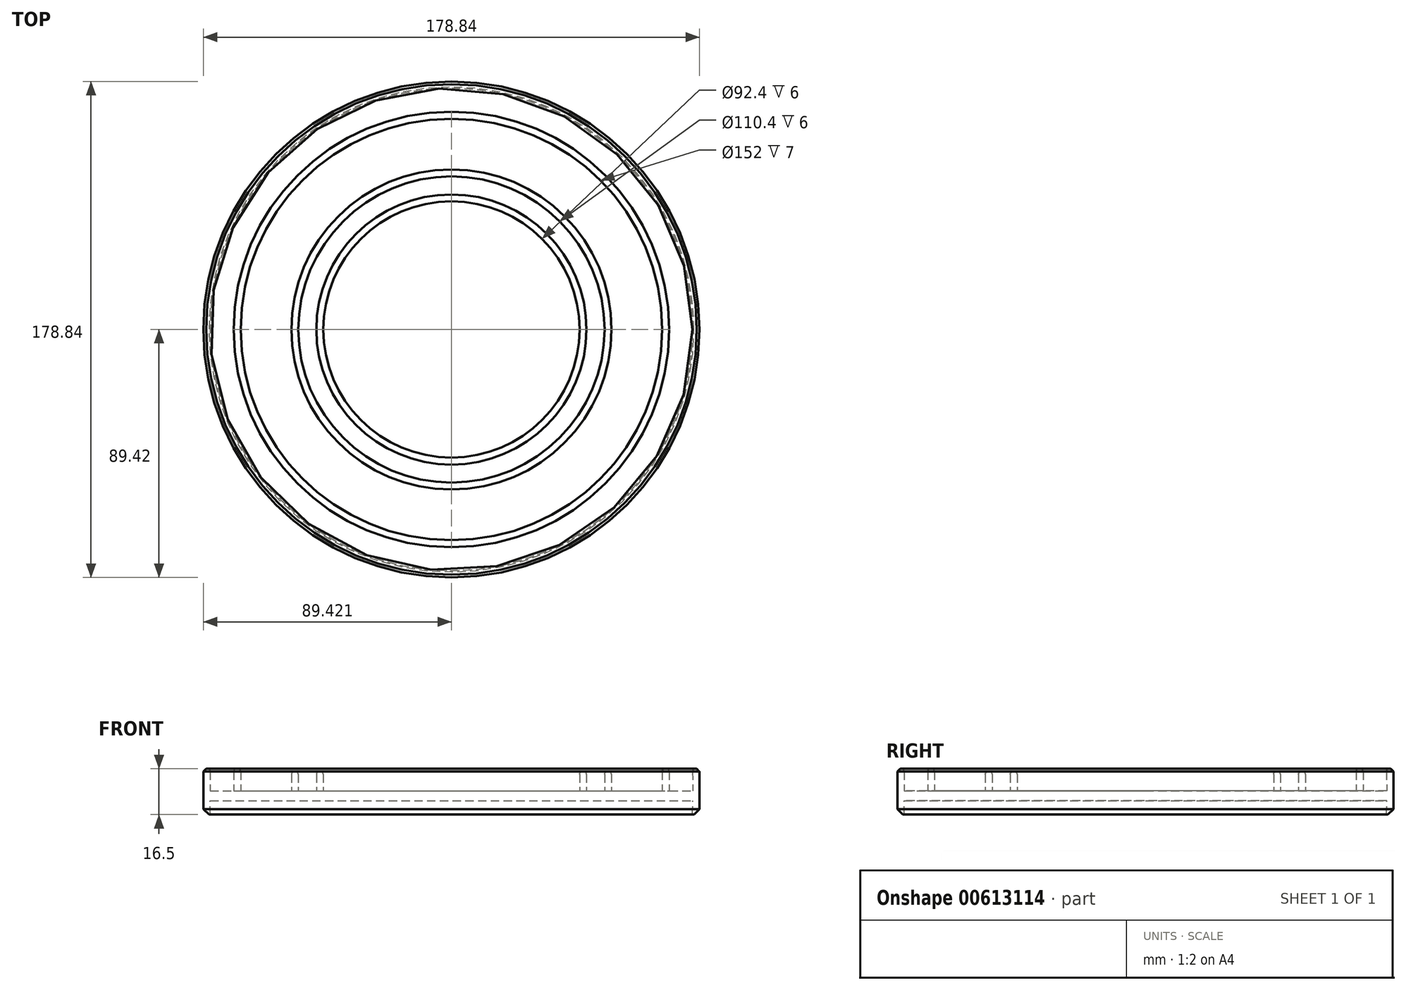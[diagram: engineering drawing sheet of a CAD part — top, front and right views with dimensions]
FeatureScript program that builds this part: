
annotation { "Feature Type Name" : "Feature", "Feature Type Description" : "" }
export const myFeature = defineFeature(function(context is Context, id is Id, definition is map)
    precondition{}
    {
        {
            var Q0;
            Q0=qCreatedBy(makeId("Front.planeOp"),FACE);
            var sketch = newSketch(context, id + "F0", { "sketchPlane" : qUnion([Q0])});
            skLineSegment(sketch, "E0", {"start": v(-51.63, -13.29) * mm, "end": v(-51.63, -9.79) * mm});
            skLineSegment(sketch, "E1", {"start": v(-51.63, -9.79) * mm, "end": v(-51.63, -1.79) * mm});
            skLineSegment(sketch, "E2", {"start": v(-51.63, -1.79) * mm, "end": v(-49.13, -1.79) * mm});
            skLineSegment(sketch, "E3", {"start": v(-49.2, -13.29) * mm, "end": v(37.8, -13.29) * mm});
            skLineSegment(sketch, "E4", {"start": v(37.8, -13.29) * mm, "end": v(37.8, -9.79) * mm});
            skLineSegment(sketch, "E5", {"start": v(37.8, -9.79) * mm, "end": v(-8.4, -9.79) * mm});
            skLineSegment(sketch, "E6", {"start": v(-8.4, -9.79) * mm, "end": v(-8.4, -2.79) * mm});
            skLineSegment(sketch, "E7", {"start": v(-8.4, -2.79) * mm, "end": v(-10.9, -2.79) * mm});
            skLineSegment(sketch, "E8", {"start": v(-10.9, -2.79) * mm, "end": v(-10.9, -9.79) * mm});
            skLineSegment(sketch, "E9", {"start": v(-10.9, -9.79) * mm, "end": v(-17.4, -9.79) * mm});
            skLineSegment(sketch, "E10", {"start": v(-17.4, -9.79) * mm, "end": v(-17.4, -2.79) * mm});
            skLineSegment(sketch, "E11", {"start": v(-17.4, -2.79) * mm, "end": v(-19.9, -2.79) * mm});
            skLineSegment(sketch, "E12", {"start": v(-19.9, -2.79) * mm, "end": v(-19.9, -9.79) * mm});
            skLineSegment(sketch, "E13", {"start": v(-19.9, -9.79) * mm, "end": v(-38.2, -9.79) * mm});
            skLineSegment(sketch, "E14", {"start": v(-38.2, -9.79) * mm, "end": v(-38.2, -1.79) * mm});
            skLineSegment(sketch, "E15", {"start": v(-38.2, -1.79) * mm, "end": v(-40.7, -1.79) * mm});
            skLineSegment(sketch, "E16", {"start": v(-40.7, -1.79) * mm, "end": v(-40.7, -9.79) * mm});
            skLineSegment(sketch, "E17", {"start": v(-40.7, -9.79) * mm, "end": v(-49.2, -9.79) * mm});
            skLineSegment(sketch, "E18", {"start": v(-49.13, -1.79) * mm, "end": v(-49.2, -9.79) * mm});
            skLineSegment(sketch, "E19", {"start": v(-51.63, -13.29) * mm, "end": v(-51.63, -18.29) * mm});
            skLineSegment(sketch, "E20", {"start": v(-51.63, -18.29) * mm, "end": v(-49.13, -18.29) * mm});
            skLineSegment(sketch, "E21", {"start": v(-49.13, -18.29) * mm, "end": v(-49.2, -13.29) * mm});
            skSolve(sketch);
        }
        {
            var Q0;
            Q0=makeQuery(id+"F0.imprint","IMPRINT",FACE,{"disambiguationData":[TD([[makeQuery(id+"F0.imprint","IMPRINT",EDGE,{"derivedFrom":sQuery(id+"F0.wireOp",EDGE,"E0")}),-1.0]])]});
            var Q1;
            Q1=sQuery(id+"F0.wireOp",EDGE,"E4");
            revolve(context, id + "F1", {"entities" : qUnion([Q0]), "axis" : qUnion([Q1]), "revolveType" : RevolveType.FULL});
        }
        {
            var Q0;
            Q0=makeQuery(id+"F1.opRevolve","SWEPT_EDGE",EDGE,{"disambiguationData":[OSD([sQuery(id+"F0.wireOp",EDGE,"E1"),sQuery(id+"F0.wireOp",EDGE,"E2")])]});
            chamfer(context, id + "F2", {"entities" : qUnion([Q0]), "width" : 1 * mm, "tangentPropagation" : true});
        }
        {
            var Q0;
            Q0=makeQuery(id+"F1.opRevolve","SWEPT_EDGE",EDGE,{"disambiguationData":[OSD([sQuery(id+"F0.wireOp",EDGE,"E2"),sQuery(id+"F0.wireOp",EDGE,"E18")])]});
            var Q1;
            Q1=makeQuery(id+"F1.opRevolve","SWEPT_FACE",FACE,{"disambiguationData":[OSD([sQuery(id+"F0.wireOp",EDGE,"E15")])]});
            var Q2;
            Q2=makeQuery(id+"F1.opRevolve","SWEPT_EDGE",EDGE,{"disambiguationData":[OSD([sQuery(id+"F0.wireOp",EDGE,"E11"),sQuery(id+"F0.wireOp",EDGE,"E12")])]});
            var Q3;
            Q3=makeQuery(id+"F1.opRevolve","SWEPT_EDGE",EDGE,{"disambiguationData":[OSD([sQuery(id+"F0.wireOp",EDGE,"E7"),sQuery(id+"F0.wireOp",EDGE,"E8")])]});
            var Q4;
            Q4=makeQuery(id+"F1.opRevolve","SWEPT_EDGE",EDGE,{"disambiguationData":[OSD([sQuery(id+"F0.wireOp",EDGE,"E6"),sQuery(id+"F0.wireOp",EDGE,"E7")])]});
            var Q5;
            Q5=makeQuery(id+"F1.opRevolve","SWEPT_EDGE",EDGE,{"disambiguationData":[OSD([sQuery(id+"F0.wireOp",EDGE,"E10"),sQuery(id+"F0.wireOp",EDGE,"E11")])]});
            fillet(context, id + "F3", {"entities" : qUnion([Q0, Q1, Q2, Q3, Q4, Q5]), "radius" : 1 * mm, "tangentPropagation" : true, "allowEdgeOverflow" : false});
        }
        {
            var Q0;
            Q0=makeQuery(id+"F1.opRevolve","SWEPT_EDGE",EDGE,{"disambiguationData":[OSD([sQuery(id+"F0.wireOp",EDGE,"E19"),sQuery(id+"F0.wireOp",EDGE,"E20")])]});
            chamfer(context, id + "F4", {"entities" : qUnion([Q0]), "width" : 2 * mm, "tangentPropagation" : true});
        }
    });
